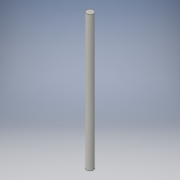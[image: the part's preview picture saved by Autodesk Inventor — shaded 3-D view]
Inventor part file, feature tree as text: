
AUTODESK INVENTOR PART (.ipt)
format: ipt  version: 2016 (Build 200138000, 138)  size: 85,504 bytes
history: native  units: in
note: dims shown in document units (in); Inventor stores cm internally (conversion verified against a paired STEP export)
features: extrude x1, sketch x1
ambient origin geometry x8: Origin, YZ Plane, XZ Plane, XY Plane, X Axis, Y Axis, Z Axis, Center Point
bodies: Solid1 (feature_tree)
feature tree (2):
  extrude  "Extrusion1"  Depth=15.748in TaperAngle=0.0deg
  sketch  "Sketch1"  dims[d2=0.7874in d3=15.748in d4=0.0in]
